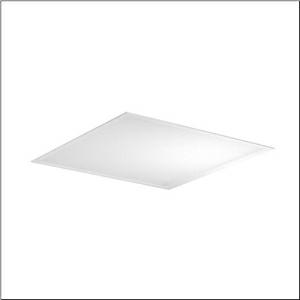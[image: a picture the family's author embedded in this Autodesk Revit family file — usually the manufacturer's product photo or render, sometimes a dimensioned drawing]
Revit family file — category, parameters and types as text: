
# Revit family: apollon_r__31_square_51mp12wd2442_6000
name_source: partatom
category: Lighting Fixtures
units: mm (PartAtom-declared; Revit-internal decimal feet)

## family parameters
Cut with Voids When Loaded = No
Host = Face
Light Source = No
Part Type = Normal
Room Calculation Point = No
Round Connector Dimension = Use Diameter
Shared = No

## types (1)
- Apollon® 31 square (1 x LED, 3800 lm, 27.5 W, 4000K)
    Apparent Load = 28 VA
    CIE Flux Codes = 61 87 97 100 100
    Color Rendering = 80
    Color Temperature = 4000K
    Default Elevation = 1800 mm
    Description = Apollon® 31 square, office luminaire, primary optical cover: micro prismatic cover, of PMMA, CAT 2 (L<= 3000cd/m²), light emission: direct distribution, primary light characteristic: symmetric, installation type: lay-in mounting, LED, rated luminous flux: 3.800lm, luminous efficacy: 138lm/W, light colour: 840, colour temperature: 4000K, control gear: DALI 2, Multilumen, with terminal, 5-pole, mains connection: 220..240V, AC/DC, 0/50..60Hz, rated input power: 28W, suitable for self-contained emergency lighting element 58DB00B013A with integrated self-test function according to EN 60598-2-22, housing, of aluminium, traffic white (RAL 9016), module: M600, length: 595mm, width: 595mm, height: 62mm, recess depth: 180mm, housing upper side, of sheet steel, coated, protection rating (complete): IP20, protection rating (on room side): IP40, insulation class (complete): insulation class II (safety insulation), certification: CE, ENEC, impact resistance: IK03, permissible operating ambient temperature: -20..+40°C, permissible storage temperature: -20..+60°C, standard: EN 60598-2-22, packaging unit: 1 piece
    Height = 0 mm  [stored 0 ft]
    Lamp = 1 x LED
    Lamp Light Flux = 3800 lm
    Lamp Power = 27.5 W
    Lamp count = 1
    Length = 595 mm
    Luminous efficacy = 138 lm/W
    Manufacturer = Siteco
    ModVariant = No
    Model = 51MP12WD2442
    Mounting Place = Ceiling
    Mounting Type = Recessed
    Number of Poles = 1
    OnlyDefault = Yes
    Power Factor = 1
    Product Name = Apollon® 31 square
    Product group = office luminaire | ceiling recessed
    ProductGroupID = 400
    Protection Class = Protection class II
    Protection Degree = IP 20
    RLX_Detail_Level = 1
    RLX_Emergency_Light_Flux = 0 lm
    RLX_Emergency_Type = 0
    RLX_Emergency_Type_DB = No
    RlxData = <blob elided: 12713 chars, md5=d168682c>
    Socket = socket
    Standby Power = 0 W
    System Light Flux = 3800 lm
    System Power = 28 W
    Type Comments = Product without accessories
    Type Image = l_1291035.jpg
    URL = http://relux.com
    VarID = ---
    Voltage = 0 V
    Weight = 0.00 kg
    Width = 595 mm

note: [stored X ft] marks values corroborated as IEEE doubles in the binary element streams (Revit-internal decimal feet)

## geometry (parser evidence)
native form markers: Sweep x11
no freeform markers — native parametric forms only
